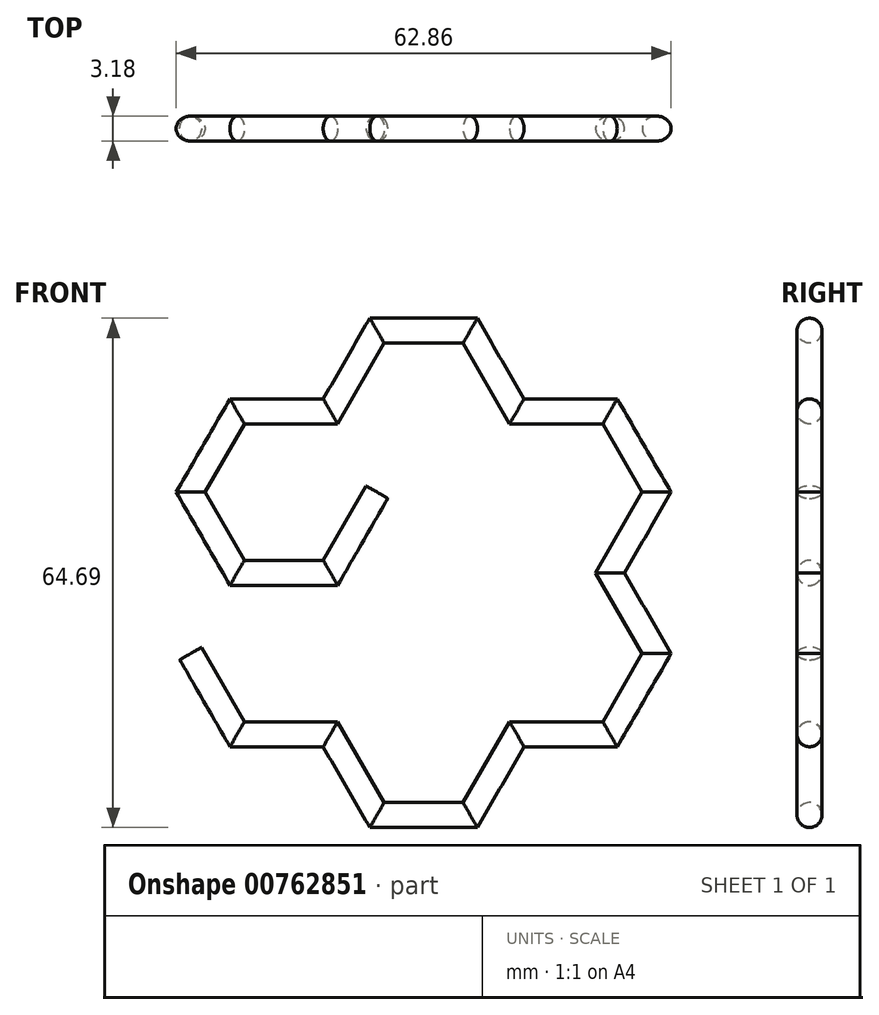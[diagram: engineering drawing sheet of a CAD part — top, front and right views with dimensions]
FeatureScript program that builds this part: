
annotation { "Feature Type Name" : "Feature", "Feature Type Description" : "" }
export const myFeature = defineFeature(function(context is Context, id is Id, definition is map)
    precondition{}
    {
        {
            var Q0;
            Q0=qCreatedBy(makeId("Front.planeOp"),FACE);
            var sketch = newSketch(context, id + "F0", { "sketchPlane" : qUnion([Q0])});
            skCircle(sketch, "E0.cCircle", {"center": v(0, 0) * mm, "radius": 10.25 * mm, "construction": true});
            skLineSegment(sketch, "E0.0", {"start": v(-5.92, 10.25) * mm, "end": v(5.92, 10.25) * mm});
            skLineSegment(sketch, "E0.1", {"start": v(5.92, 10.25) * mm, "end": v(11.84, 0) * mm});
            skLineSegment(sketch, "E0.2", {"start": v(11.84, 0) * mm, "end": v(5.92, -10.25) * mm});
            skLineSegment(sketch, "E0.3", {"start": v(5.92, -10.25) * mm, "end": v(-5.92, -10.25) * mm});
            skLineSegment(sketch, "E0.4", {"start": v(-5.92, -10.25) * mm, "end": v(-11.84, 0) * mm});
            skLineSegment(sketch, "E0.5", {"start": v(-11.84, 0) * mm, "end": v(-5.92, 10.25) * mm});
            skPoint(sketch, "E0.0.midPoint", {"position": v(0, 10.25) * mm});
            skCircle(sketch, "E1.cCircle", {"center": v(17.76, -10.25) * mm, "radius": 10.25 * mm, "construction": true});
            skLineSegment(sketch, "E1.0", {"start": v(11.84, 0) * mm, "end": v(23.68, 0) * mm});
            skLineSegment(sketch, "E1.1", {"start": v(23.68, 0) * mm, "end": v(29.6, -10.25) * mm});
            skLineSegment(sketch, "E1.2", {"start": v(29.6, -10.25) * mm, "end": v(23.68, -20.5) * mm});
            skLineSegment(sketch, "E1.3", {"start": v(23.68, -20.5) * mm, "end": v(11.84, -20.5) * mm});
            skLineSegment(sketch, "E1.4", {"start": v(11.84, -20.5) * mm, "end": v(5.92, -10.25) * mm});
            skLineSegment(sketch, "E1.5", {"start": v(5.92, -10.25) * mm, "end": v(11.84, 0) * mm});
            skPoint(sketch, "E1.0.midPoint", {"position": v(17.76, 0) * mm});
            skCircle(sketch, "E2.cCircle", {"center": v(17.76, 10.25) * mm, "radius": 10.25 * mm, "construction": true});
            skLineSegment(sketch, "E2.0", {"start": v(11.84, 20.5) * mm, "end": v(23.68, 20.5) * mm});
            skLineSegment(sketch, "E2.1", {"start": v(23.68, 20.5) * mm, "end": v(29.6, 10.25) * mm});
            skLineSegment(sketch, "E2.2", {"start": v(29.6, 10.25) * mm, "end": v(23.68, 0) * mm});
            skLineSegment(sketch, "E2.3", {"start": v(23.68, 0) * mm, "end": v(11.84, 0) * mm});
            skLineSegment(sketch, "E2.4", {"start": v(11.84, 0) * mm, "end": v(5.92, 10.25) * mm});
            skLineSegment(sketch, "E2.5", {"start": v(5.92, 10.25) * mm, "end": v(11.84, 20.5) * mm});
            skPoint(sketch, "E2.0.midPoint", {"position": v(17.76, 20.5) * mm});
            skCircle(sketch, "E3.cCircle", {"center": v(35.52, 0) * mm, "radius": 10.25 * mm, "construction": true});
            skLineSegment(sketch, "E3.0", {"start": v(29.6, 10.25) * mm, "end": v(41.44, 10.25) * mm});
            skLineSegment(sketch, "E3.1", {"start": v(41.44, 10.25) * mm, "end": v(47.36, 0) * mm});
            skLineSegment(sketch, "E3.2", {"start": v(47.36, 0) * mm, "end": v(41.44, -10.25) * mm});
            skLineSegment(sketch, "E3.3", {"start": v(41.44, -10.25) * mm, "end": v(29.6, -10.25) * mm});
            skLineSegment(sketch, "E3.4", {"start": v(29.6, -10.25) * mm, "end": v(23.68, 0) * mm});
            skLineSegment(sketch, "E3.5", {"start": v(23.68, 0) * mm, "end": v(29.6, 10.25) * mm});
            skPoint(sketch, "E3.0.midPoint", {"position": v(35.52, 10.25) * mm});
            skCircle(sketch, "E4.cCircle", {"center": v(0, 20.5) * mm, "radius": 10.25 * mm, "construction": true});
            skLineSegment(sketch, "E4.0", {"start": v(-5.92, 30.76) * mm, "end": v(5.92, 30.76) * mm});
            skLineSegment(sketch, "E4.1", {"start": v(5.92, 30.76) * mm, "end": v(11.84, 20.5) * mm});
            skLineSegment(sketch, "E4.2", {"start": v(11.84, 20.5) * mm, "end": v(5.92, 10.25) * mm});
            skLineSegment(sketch, "E4.3", {"start": v(5.92, 10.25) * mm, "end": v(-5.92, 10.25) * mm});
            skLineSegment(sketch, "E4.4", {"start": v(-5.92, 10.25) * mm, "end": v(-11.84, 20.5) * mm});
            skLineSegment(sketch, "E4.5", {"start": v(-11.84, 20.5) * mm, "end": v(-5.92, 30.76) * mm});
            skPoint(sketch, "E4.0.midPoint", {"position": v(0, 30.76) * mm});
            skCircle(sketch, "E5.cCircle", {"center": v(17.76, 30.76) * mm, "radius": 10.25 * mm, "construction": true});
            skLineSegment(sketch, "E5.0", {"start": v(11.84, 41.01) * mm, "end": v(23.68, 41.01) * mm});
            skLineSegment(sketch, "E5.1", {"start": v(23.68, 41.01) * mm, "end": v(29.6, 30.76) * mm});
            skLineSegment(sketch, "E5.2", {"start": v(29.6, 30.76) * mm, "end": v(23.68, 20.5) * mm});
            skLineSegment(sketch, "E5.3", {"start": v(23.68, 20.5) * mm, "end": v(11.84, 20.5) * mm});
            skLineSegment(sketch, "E5.4", {"start": v(11.84, 20.5) * mm, "end": v(5.92, 30.76) * mm});
            skLineSegment(sketch, "E5.5", {"start": v(5.92, 30.76) * mm, "end": v(11.84, 41.01) * mm});
            skPoint(sketch, "E5.0.midPoint", {"position": v(17.76, 41.01) * mm});
            skCircle(sketch, "E6.cCircle", {"center": v(35.52, 20.5) * mm, "radius": 10.25 * mm, "construction": true});
            skLineSegment(sketch, "E6.0", {"start": v(29.6, 30.76) * mm, "end": v(41.44, 30.76) * mm});
            skLineSegment(sketch, "E6.1", {"start": v(41.44, 30.76) * mm, "end": v(47.36, 20.5) * mm});
            skLineSegment(sketch, "E6.2", {"start": v(47.36, 20.5) * mm, "end": v(41.44, 10.25) * mm});
            skLineSegment(sketch, "E6.3", {"start": v(41.44, 10.25) * mm, "end": v(29.6, 10.25) * mm});
            skLineSegment(sketch, "E6.4", {"start": v(29.6, 10.25) * mm, "end": v(23.68, 20.5) * mm});
            skLineSegment(sketch, "E6.5", {"start": v(23.68, 20.5) * mm, "end": v(29.6, 30.76) * mm});
            skPoint(sketch, "E6.0.midPoint", {"position": v(35.52, 30.76) * mm});
            skSolve(sketch);
        }
        {
            var Q0;
            Q0=qCreatedBy(makeId("Right.planeOp"),FACE);
            var sketch = newSketch(context, id + "F1", { "sketchPlane" : qUnion([Q0])});
            skCircle(sketch, "E7", {"center": v(0, 10.25) * mm, "radius": 1.59 * mm});
            skSolve(sketch);
        }
        {
            var Q0;
            Q0=makeQuery(id+"F1.imprint","IMPRINT",FACE,{"disambiguationData":[TD([[makeQuery(id+"F1.imprint","IMPRINT",EDGE,{"derivedFrom":sQuery(id+"F1.wireOp",EDGE,"E7")}),1.0]])]});
            var Q1;
            Q1=sQuery(id+"F0.wireOp",EDGE,"E4.3");
            var Q2;
            Q2=sQuery(id+"F0.wireOp",EDGE,"E4.4");
            var Q3;
            Q3=sQuery(id+"F0.wireOp",EDGE,"E4.5");
            var Q4;
            Q4=sQuery(id+"F0.wireOp",EDGE,"E4.0");
            var Q5;
            Q5=sQuery(id+"F0.wireOp",EDGE,"E4.2");
            var Q6;
            Q6=sQuery(id+"F0.wireOp",EDGE,"E5.5");
            var Q7;
            Q7=sQuery(id+"F0.wireOp",EDGE,"E5.0");
            var Q8;
            Q8=sQuery(id+"F0.wireOp",EDGE,"E5.1");
            var Q9;
            Q9=sQuery(id+"F0.wireOp",EDGE,"E6.0");
            var Q10;
            Q10=sQuery(id+"F0.wireOp",EDGE,"E6.1");
            var Q11;
            Q11=sQuery(id+"F0.wireOp",EDGE,"E6.2");
            var Q12;
            Q12=sQuery(id+"F0.wireOp",EDGE,"E3.1");
            var Q13;
            Q13=sQuery(id+"F0.wireOp",EDGE,"E3.2");
            var Q14;
            Q14=sQuery(id+"F0.wireOp",EDGE,"E3.3");
            var Q15;
            Q15=sQuery(id+"F0.wireOp",EDGE,"E1.2");
            var Q16;
            Q16=sQuery(id+"F0.wireOp",EDGE,"E1.3");
            var Q17;
            Q17=sQuery(id+"F0.wireOp",EDGE,"E1.4");
            var Q18;
            Q18=sQuery(id+"F0.wireOp",EDGE,"E0.3");
            var Q19;
            Q19=sQuery(id+"F0.wireOp",EDGE,"E0.4");
            sweep(context, id + "F2", {"profiles" : qUnion([Q0]), "path" : qUnion([Q1, Q2, Q3, Q4, Q5, Q6, Q7, Q8, Q9, Q10, Q11, Q12, Q13, Q14, Q15, Q16, Q17, Q18, Q19])});
        }
    });
